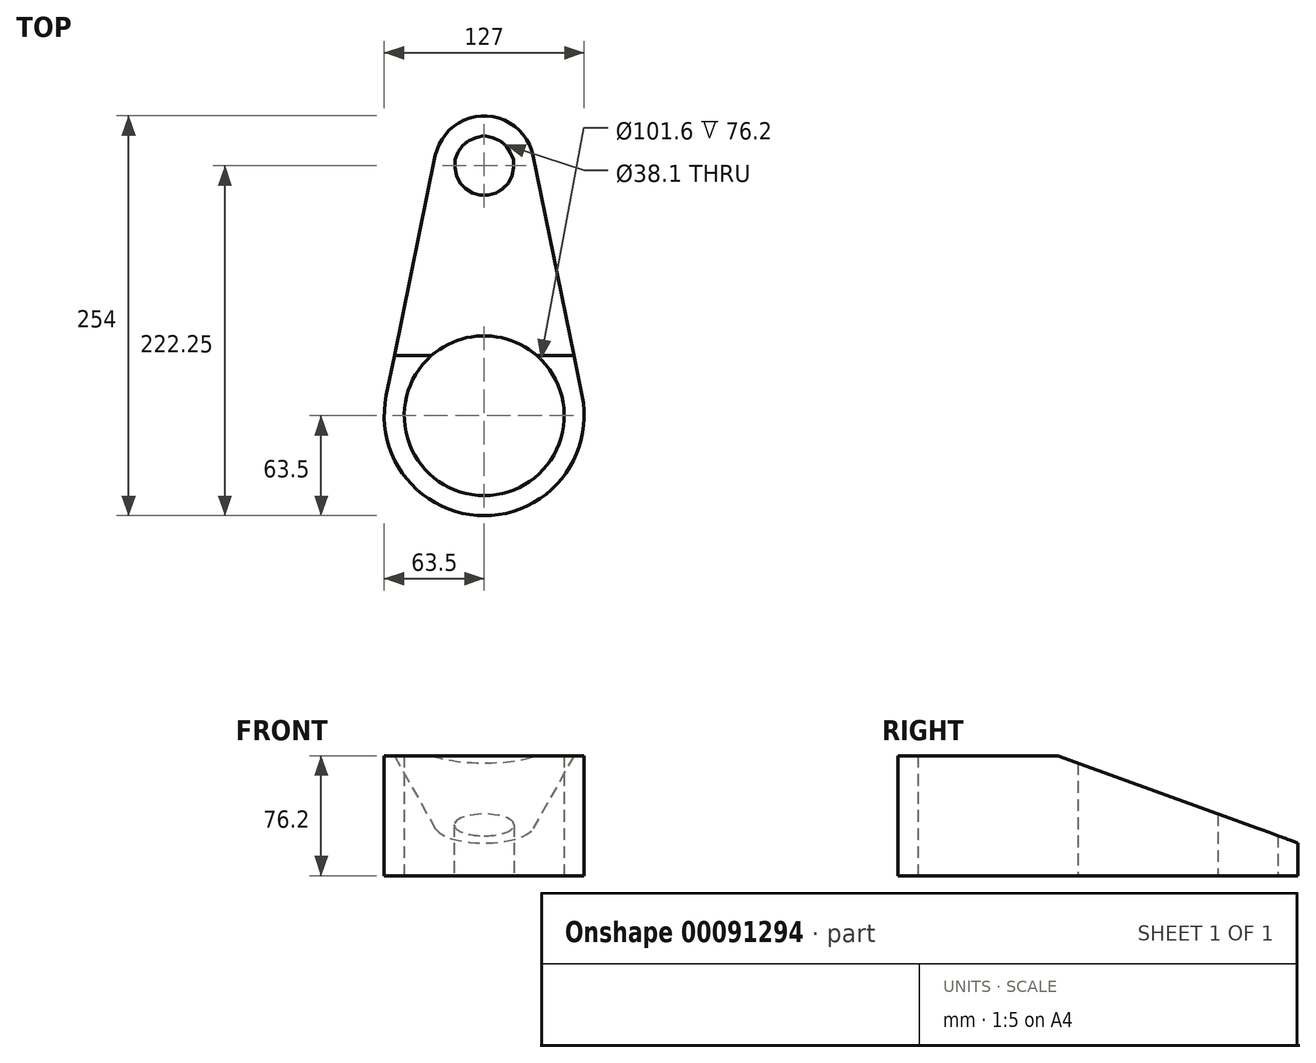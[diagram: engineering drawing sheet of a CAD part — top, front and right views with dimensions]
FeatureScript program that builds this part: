
annotation { "Feature Type Name" : "Feature", "Feature Type Description" : "" }
export const myFeature = defineFeature(function(context is Context, id is Id, definition is map)
    precondition{}
    {
        {
            var Q0;
            Q0=qCreatedBy(makeId("Top.planeOp"),FACE);
            var sketch = newSketch(context, id + "F0", { "sketchPlane" : qUnion([Q0])});
            skCircle(sketch, "E0", {"center": v(0, 0) * mm, "radius": 63.5 * mm});
            skCircle(sketch, "E1", {"center": v(0, 0) * mm, "radius": 50.8 * mm});
            skCircle(sketch, "E2", {"center": v(0, 158.75) * mm, "radius": 19.05 * mm});
            skCircle(sketch, "E3", {"center": v(0, 158.75) * mm, "radius": 31.75 * mm});
            skLineSegment(sketch, "E4", {"start": v(-31.1, 165.1) * mm, "end": v(-62.22, 12.7) * mm});
            skLineSegment(sketch, "E5", {"start": v(31.1, 165.1) * mm, "end": v(62.22, 12.7) * mm});
            skSolve(sketch);
        }
        {
            var Q0;
            Q0 = qSketchRegion(id + "F0", true);
            extrude(context, id + "F1", {"entities" : qUnion([Q0]), "depth" : 76.2 * mm});
        }
        {
            var Q0;
            Q0=qCreatedBy(makeId("Right.planeOp"),FACE);
            var sketch = newSketch(context, id + "F2", { "sketchPlane" : qUnion([Q0])});
            skLineSegment(sketch, "E6", {"start": v(0, 0) * mm, "end": v(0, 76.47) * mm, "construction": true});
            skPoint(sketch, "E7.0", {"position": v(12.7, 76.2) * mm});
            skLineSegment(sketch, "E8", {"start": v(38.1, 76.2) * mm, "end": v(220.37, 9.86) * mm});
            skLineSegment(sketch, "E9", {"start": v(220.37, 9.86) * mm, "end": v(220.37, 76.2) * mm});
            skLineSegment(sketch, "E10", {"start": v(220.37, 76.2) * mm, "end": v(38.1, 76.2) * mm});
            skSolve(sketch);
        }
        {
            var Q0;
            Q0 = qSketchRegion(id + "F2", true);
            extrude(context, id + "F3", {"entities" : qUnion([Q0]), "operationType" : NewBodyOperationType.REMOVE, "endBound" : BoundingType.SYMMETRIC, "oppositeDirection" : true, "depth" : 127 * mm});
        }
    });
